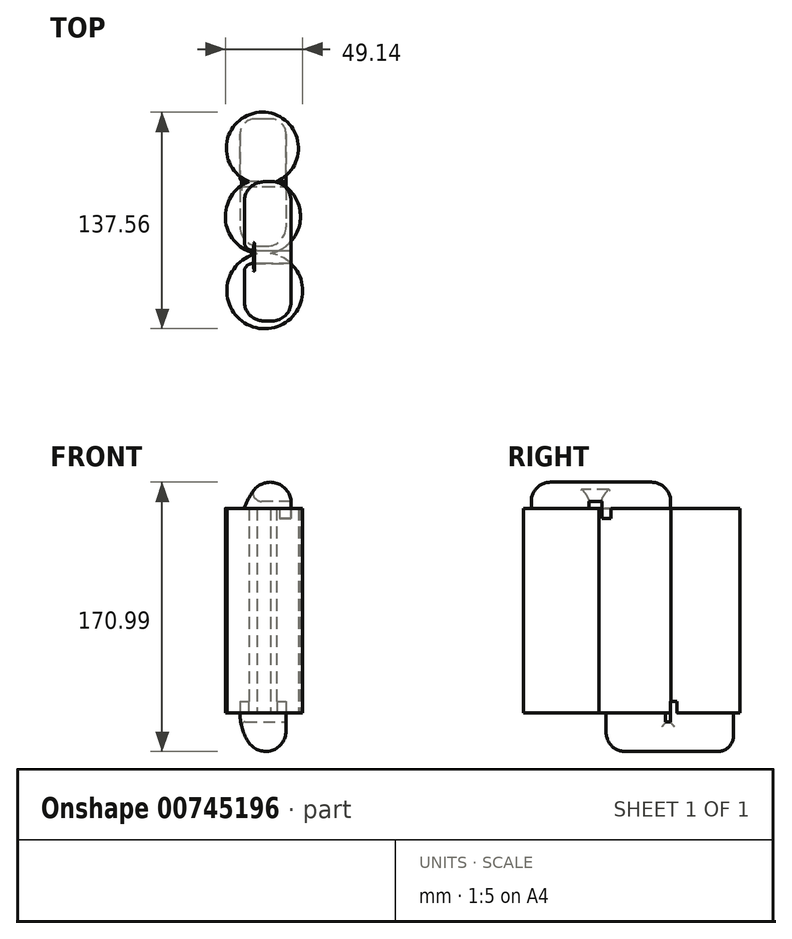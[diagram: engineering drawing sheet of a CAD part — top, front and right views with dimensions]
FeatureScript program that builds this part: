
annotation { "Feature Type Name" : "Feature", "Feature Type Description" : "" }
export const myFeature = defineFeature(function(context is Context, id is Id, definition is map)
    precondition{}
    {
        {
            var Q0;
            Q0=qCreatedBy(makeId("Top.planeOp"),FACE);
            var sketch = newSketch(context, id + "F0", { "sketchPlane" : qUnion([Q0])});
            skCircle(sketch, "E0", {"center": v(-33.88, 48.45) * mm, "radius": 22.9 * mm});
            skSolve(sketch);
        }
        {
            var Q0;
            Q0 = qSketchRegion(id + "F0", true);
            extrude(context, id + "F1", {"entities" : qUnion([Q0]), "depth" : 130 * mm, "offsetDistance" : 25 * mm});
        }
        {
            var Q0;
            Q0=qCreatedBy(makeId("Top.planeOp"),FACE);
            var sketch = newSketch(context, id + "F2", { "sketchPlane" : qUnion([Q0])});
            skCircle(sketch, "E1", {"center": v(-33.58, 5.08) * mm, "radius": 23.9 * mm});
            skSolve(sketch);
        }
        {
            var Q0;
            Q0 = qSketchRegion(id + "F2", true);
            extrude(context, id + "F3", {"entities" : qUnion([Q0]), "operationType" : NewBodyOperationType.ADD, "depth" : 105 * mm, "offsetDistance" : 25 * mm});
        }
        {
            var Q0;
            Q0=makeQuery(id+"F3.opExtrude","CAP_FACE",FACE,{"disambiguationData":[OSD([sQuery(id+"F2.wireOp",EDGE,"E1")])],"isStart":false});
            var sketch = newSketch(context, id + "F4", { "sketchPlane" : qUnion([Q0])});
            skCircle(sketch, "E2", {"center": v(-33.58, 5.08) * mm, "radius": 23.9 * mm});
            skSolve(sketch);
        }
        {
            var Q0;
            {var subQ1=makeQuery(id+"F3.boolean.opBoolean","INTERSECT",EDGE,{"derivedFrom":[makeQuery(id+"F1.opExtrude","SWEPT_FACE",FACE,{"disambiguationData":[OSD([sQuery(id+"F0.wireOp",EDGE,"E0")])]}),makeQuery(id+"F3.opExtrude","CAP_FACE",FACE,{"disambiguationData":[OSD([sQuery(id+"F2.wireOp",EDGE,"E1")])],"isStart":false})]});Q0=makeQuery(id+"F4.imprint","IMPRINT",FACE,{"disambiguationData":[TD([[makeQuery(id+"F4.imprint","IMPRINT",EDGE,{"derivedFrom":subQ1}),-1.0]])]});}
            extrude(context, id + "F5", {"entities" : qUnion([Q0]), "operationType" : NewBodyOperationType.ADD, "depth" : 25 * mm, "offsetDistance" : 25 * mm});
        }
        {
            var Q0;
            Q0=qCreatedBy(makeId("Top.planeOp"),FACE);
            var sketch = newSketch(context, id + "F6", { "sketchPlane" : qUnion([Q0])});
            skCircle(sketch, "E3", {"center": v(-32.4, -42.13) * mm, "radius": 24.08 * mm});
            skSolve(sketch);
        }
        {
            var Q0;
            Q0 = qSketchRegion(id + "F6", true);
            extrude(context, id + "F7", {"entities" : qUnion([Q0]), "operationType" : NewBodyOperationType.ADD, "depth" : 130 * mm, "offsetDistance" : 25 * mm});
        }
        {
            var Q0;
            {var subQ0=sQuery(id+"F0.wireOp",EDGE,"E0");Q0=makeQuery(id+"F7.boolean.opBoolean","MERGE",FACE,{"derivedFrom":[makeQuery(id+"F5.boolean.opBoolean","MERGE",FACE,{"derivedFrom":[makeQuery(id+"F1.opExtrude","CAP_FACE",FACE,{"disambiguationData":[OSD([subQ0])],"isStart":false}),makeQuery(id+"F5.opExtrude","CAP_FACE",FACE,{"disambiguationData":[OSD([subQ0,sQuery(id+"F2.wireOp",EDGE,"E1"),sQuery(id+"F4.wireOp",EDGE,"E2")])],"isStart":false})]}),makeQuery(id+"F7.opExtrude","CAP_FACE",FACE,{"disambiguationData":[OSD([sQuery(id+"F6.wireOp",EDGE,"E3")])],"isStart":false})]});}
            var sketch = newSketch(context, id + "F8", { "sketchPlane" : qUnion([Q0])});
            skLineSegment(sketch, "E4.bottom", {"start": v(-46.96, -61.31) * mm, "end": v(-15.68, -61.31) * mm});
            skLineSegment(sketch, "E4.top", {"start": v(-46.96, -24.82) * mm, "end": v(-15.68, -24.82) * mm});
            skLineSegment(sketch, "E4.left", {"start": v(-46.96, -61.31) * mm, "end": v(-46.96, -24.82) * mm});
            skLineSegment(sketch, "E4.right", {"start": v(-15.68, -61.31) * mm, "end": v(-15.68, -24.82) * mm});
            skSolve(sketch);
        }
        {
            var Q0;
            Q0 = qSketchRegion(id + "F8", true);
            extrude(context, id + "F9", {"entities" : qUnion([Q0]), "operationType" : NewBodyOperationType.ADD, "depth" : 28 * mm, "offsetDistance" : 25 * mm});
        }
        {
            var Q0;
            Q0=makeQuery(id+"F9.opExtrude","SWEPT_FACE",FACE,{"disambiguationData":[OSD([sQuery(id+"F8.wireOp",EDGE,"E4.top")])]});
            var sketch = newSketch(context, id + "F10", { "sketchPlane" : qUnion([Q0])});
            skLineSegment(sketch, "E5.bottom", {"start": v(15.68, 158) * mm, "end": v(46.96, 158) * mm});
            skLineSegment(sketch, "E5.top", {"start": v(15.68, 134.5) * mm, "end": v(46.96, 134.5) * mm});
            skLineSegment(sketch, "E5.left", {"start": v(15.68, 158) * mm, "end": v(15.68, 134.5) * mm});
            skLineSegment(sketch, "E5.right", {"start": v(46.96, 158) * mm, "end": v(46.96, 134.5) * mm});
            skSolve(sketch);
        }
        {
            var Q0;
            Q0 = qSketchRegion(id + "F10", true);
            extrude(context, id + "F11", {"entities" : qUnion([Q0]), "operationType" : NewBodyOperationType.ADD, "depth" : 52 * mm, "offsetDistance" : 25 * mm});
        }
        {
            var Q0;
            Q0=makeQuery(id+"F11.opExtrude","SWEPT_FACE",FACE,{"disambiguationData":[OSD([sQuery(id+"F10.wireOp",EDGE,"E5.top")])]});
            var sketch = newSketch(context, id + "F12", { "sketchPlane" : qUnion([Q0])});
            skLineSegment(sketch, "E6.bottom", {"start": v(-46.96, -27.18) * mm, "end": v(-15.68, -27.18) * mm});
            skLineSegment(sketch, "E6.top", {"start": v(-46.96, 16.43) * mm, "end": v(-15.68, 16.43) * mm});
            skLineSegment(sketch, "E6.left", {"start": v(-46.96, -27.18) * mm, "end": v(-46.96, 16.43) * mm});
            skLineSegment(sketch, "E6.right", {"start": v(-15.68, -27.18) * mm, "end": v(-15.68, 16.43) * mm});
            skSolve(sketch);
        }
        {
            var Q0;
            Q0 = qSketchRegion(id + "F12", true);
            extrude(context, id + "F13", {"entities" : qUnion([Q0]), "operationType" : NewBodyOperationType.ADD, "depth" : 11 * mm, "offsetDistance" : 25 * mm});
        }
        {
            var Q0;
            Q0=makeQuery(id+"F11.boolean.opBoolean","MERGE",EDGE,{"derivedFrom":[makeQuery(id+"F9.opExtrude","CAP_EDGE",EDGE,{"disambiguationData":[OSD([sQuery(id+"F8.wireOp",EDGE,"E4.left")])],"isStart":false}),makeQuery(id+"F11.opExtrude","SWEPT_EDGE",EDGE,{"disambiguationData":[OSD([sQuery(id+"F10.wireOp",EDGE,"E5.bottom"),sQuery(id+"F10.wireOp",EDGE,"E5.right")])]})]});
            fillet(context, id + "F14", {"entities" : qUnion([Q0]), "radius" : 41.04 * mm, "tangentPropagation" : true, "allowEdgeOverflow" : false});
        }
        {
            var Q0;
            Q0=makeQuery(id+"F7.boolean.opBoolean","MERGE",FACE,{"derivedFrom":[makeQuery(id+"F3.boolean.opBoolean","MERGE",FACE,{"derivedFrom":[makeQuery(id+"F1.opExtrude","CAP_FACE",FACE,{"disambiguationData":[OSD([sQuery(id+"F0.wireOp",EDGE,"E0")])],"isStart":true}),makeQuery(id+"F3.opExtrude","CAP_FACE",FACE,{"disambiguationData":[OSD([sQuery(id+"F2.wireOp",EDGE,"E1")])],"isStart":true})]}),makeQuery(id+"F7.opExtrude","CAP_FACE",FACE,{"disambiguationData":[OSD([sQuery(id+"F6.wireOp",EDGE,"E3")])],"isStart":true})]});
            var sketch = newSketch(context, id + "F15", { "sketchPlane" : qUnion([Q0])});
            skLineSegment(sketch, "E7.bottom", {"start": v(-48.12, -24.03) * mm, "end": v(-18.9, -24.03) * mm});
            skLineSegment(sketch, "E7.top", {"start": v(-48.12, 13.78) * mm, "end": v(-18.9, 13.78) * mm});
            skLineSegment(sketch, "E7.left", {"start": v(-48.12, -24.03) * mm, "end": v(-48.12, 13.78) * mm});
            skLineSegment(sketch, "E7.right", {"start": v(-18.9, -24.03) * mm, "end": v(-18.9, 13.78) * mm});
            skSolve(sketch);
        }
        {
            var Q0;
            Q0 = qSketchRegion(id + "F15", true);
            extrude(context, id + "F16", {"entities" : qUnion([Q0]), "operationType" : NewBodyOperationType.ADD, "depth" : 32 * mm, "offsetDistance" : 25 * mm});
        }
        {
            var Q0;
            Q0=makeQuery(id+"F16.opExtrude","SWEPT_FACE",FACE,{"disambiguationData":[OSD([sQuery(id+"F15.wireOp",EDGE,"E7.bottom")])]});
            var sketch = newSketch(context, id + "F17", { "sketchPlane" : qUnion([Q0])});
            skLineSegment(sketch, "E8.bottom", {"start": v(48.12, -32) * mm, "end": v(18.9, -32) * mm});
            skLineSegment(sketch, "E8.top", {"start": v(48.12, -5.6) * mm, "end": v(18.9, -5.6) * mm});
            skLineSegment(sketch, "E8.left", {"start": v(48.12, -32) * mm, "end": v(48.12, -5.6) * mm});
            skLineSegment(sketch, "E8.right", {"start": v(18.9, -32) * mm, "end": v(18.9, -5.6) * mm});
            skSolve(sketch);
        }
        {
            var Q0;
            Q0 = qSketchRegion(id + "F17", true);
            extrude(context, id + "F18", {"entities" : qUnion([Q0]), "operationType" : NewBodyOperationType.ADD, "depth" : 43 * mm, "offsetDistance" : 25 * mm});
        }
        {
            var Q0;
            Q0=makeQuery(id+"F18.opExtrude","SWEPT_FACE",FACE,{"disambiguationData":[OSD([sQuery(id+"F17.wireOp",EDGE,"E8.top")])]});
            var sketch = newSketch(context, id + "F19", { "sketchPlane" : qUnion([Q0])});
            skLineSegment(sketch, "E9.bottom", {"start": v(-48.12, 67.03) * mm, "end": v(-18.9, 67.03) * mm});
            skLineSegment(sketch, "E9.top", {"start": v(-48.12, 27.18) * mm, "end": v(-18.9, 27.18) * mm});
            skLineSegment(sketch, "E9.left", {"start": v(-48.12, 67.03) * mm, "end": v(-48.12, 27.18) * mm});
            skLineSegment(sketch, "E9.right", {"start": v(-18.9, 67.03) * mm, "end": v(-18.9, 27.18) * mm});
            skSolve(sketch);
        }
        {
            var Q0;
            Q0 = qSketchRegion(id + "F19", true);
            extrude(context, id + "F20", {"entities" : qUnion([Q0]), "operationType" : NewBodyOperationType.ADD, "depth" : 13 * mm, "offsetDistance" : 25 * mm});
        }
        {
            var Q0;
            Q0=makeQuery(id+"F18.boolean.opBoolean","MERGE",EDGE,{"derivedFrom":[makeQuery(id+"F16.opExtrude","CAP_EDGE",EDGE,{"disambiguationData":[OSD([sQuery(id+"F15.wireOp",EDGE,"E7.left")])],"isStart":false}),makeQuery(id+"F18.opExtrude","SWEPT_EDGE",EDGE,{"disambiguationData":[OSD([sQuery(id+"F17.wireOp",EDGE,"E8.bottom"),sQuery(id+"F17.wireOp",EDGE,"E8.left")])]})]});
            fillet(context, id + "F21", {"entities" : qUnion([Q0]), "radius" : 31.38 * mm, "tangentPropagation" : true, "allowEdgeOverflow" : false});
        }
        {
            var Q0;
            Q0=makeQuery(id+"F21.opFillet","BLEND_EDGE",EDGE,{"blendedFrom":[makeQuery(id+"F18.boolean.opBoolean","MERGE",EDGE,{"derivedFrom":[makeQuery(id+"F16.opExtrude","CAP_EDGE",EDGE,{"disambiguationData":[OSD([sQuery(id+"F15.wireOp",EDGE,"E7.left")])],"isStart":false}),makeQuery(id+"F18.opExtrude","SWEPT_EDGE",EDGE,{"disambiguationData":[OSD([sQuery(id+"F17.wireOp",EDGE,"E8.bottom"),sQuery(id+"F17.wireOp",EDGE,"E8.left")])]})]}),makeQuery(id+"F20.boolean.opBoolean","MERGE",FACE,{"derivedFrom":[makeQuery(id+"F18.boolean.opBoolean","MERGE",FACE,{"derivedFrom":[makeQuery(id+"F16.opExtrude","SWEPT_FACE",FACE,{"disambiguationData":[OSD([sQuery(id+"F15.wireOp",EDGE,"E7.right")])]}),makeQuery(id+"F18.opExtrude","SWEPT_FACE",FACE,{"disambiguationData":[OSD([sQuery(id+"F17.wireOp",EDGE,"E8.right")])]})]}),makeQuery(id+"F20.opExtrude","SWEPT_FACE",FACE,{"disambiguationData":[OSD([sQuery(id+"F19.wireOp",EDGE,"E9.right")])]})]})],"blendedInto":[makeQuery(id+"F20.boolean.opBoolean","MERGE",FACE,{"derivedFrom":[makeQuery(id+"F18.boolean.opBoolean","MERGE",FACE,{"derivedFrom":[makeQuery(id+"F16.opExtrude","SWEPT_FACE",FACE,{"disambiguationData":[OSD([sQuery(id+"F15.wireOp",EDGE,"E7.right")])]}),makeQuery(id+"F18.opExtrude","SWEPT_FACE",FACE,{"disambiguationData":[OSD([sQuery(id+"F17.wireOp",EDGE,"E8.right")])]})]}),makeQuery(id+"F20.opExtrude","SWEPT_FACE",FACE,{"disambiguationData":[OSD([sQuery(id+"F19.wireOp",EDGE,"E9.right")])]})]})]});
            fillet(context, id + "F22", {"entities" : qUnion([Q0]), "radius" : 12.9 * mm, "tangentPropagation" : true, "allowEdgeOverflow" : false});
        }
        {
            var Q0;
            {var subQ0=sQuery(id+"F17.wireOp",EDGE,"E8.right");var subQ1=sQuery(id+"F17.wireOp",EDGE,"E8.left");var subQ2=sQuery(id+"F17.wireOp",EDGE,"E8.bottom");Q0=makeQuery(id+"F22.opFillet","BLEND_EDGE",EDGE,{"blendedFrom":[makeQuery(id+"F21.opFillet","BLEND_EDGE",EDGE,{"blendedFrom":[makeQuery(id+"F18.boolean.opBoolean","MERGE",EDGE,{"derivedFrom":[makeQuery(id+"F16.opExtrude","CAP_EDGE",EDGE,{"disambiguationData":[OSD([sQuery(id+"F15.wireOp",EDGE,"E7.left")])],"isStart":false}),makeQuery(id+"F18.opExtrude","SWEPT_EDGE",EDGE,{"disambiguationData":[OSD([subQ2,subQ1])]})]}),makeQuery(id+"F20.boolean.opBoolean","MERGE",FACE,{"derivedFrom":[makeQuery(id+"F18.boolean.opBoolean","MERGE",FACE,{"derivedFrom":[makeQuery(id+"F16.opExtrude","SWEPT_FACE",FACE,{"disambiguationData":[OSD([sQuery(id+"F15.wireOp",EDGE,"E7.right")])]}),makeQuery(id+"F18.opExtrude","SWEPT_FACE",FACE,{"disambiguationData":[OSD([subQ0])]})]}),makeQuery(id+"F20.opExtrude","SWEPT_FACE",FACE,{"disambiguationData":[OSD([sQuery(id+"F19.wireOp",EDGE,"E9.right")])]})]})],"blendedInto":[makeQuery(id+"F20.boolean.opBoolean","MERGE",FACE,{"derivedFrom":[makeQuery(id+"F18.boolean.opBoolean","MERGE",FACE,{"derivedFrom":[makeQuery(id+"F16.opExtrude","SWEPT_FACE",FACE,{"disambiguationData":[OSD([sQuery(id+"F15.wireOp",EDGE,"E7.right")])]}),makeQuery(id+"F18.opExtrude","SWEPT_FACE",FACE,{"disambiguationData":[OSD([subQ0])]})]}),makeQuery(id+"F20.opExtrude","SWEPT_FACE",FACE,{"disambiguationData":[OSD([sQuery(id+"F19.wireOp",EDGE,"E9.right")])]})]})]}),makeQuery(id+"F20.boolean.opBoolean","MERGE",FACE,{"derivedFrom":[makeQuery(id+"F18.opExtrude","CAP_FACE",FACE,{"disambiguationData":[OSD([subQ2,sQuery(id+"F17.wireOp",EDGE,"E8.top"),subQ1,subQ0])],"isStart":false}),makeQuery(id+"F20.opExtrude","SWEPT_FACE",FACE,{"disambiguationData":[OSD([sQuery(id+"F19.wireOp",EDGE,"E9.bottom")])]})]})],"blendedInto":[makeQuery(id+"F20.boolean.opBoolean","MERGE",FACE,{"derivedFrom":[makeQuery(id+"F18.opExtrude","CAP_FACE",FACE,{"disambiguationData":[OSD([subQ2,sQuery(id+"F17.wireOp",EDGE,"E8.top"),subQ1,subQ0])],"isStart":false}),makeQuery(id+"F20.opExtrude","SWEPT_FACE",FACE,{"disambiguationData":[OSD([sQuery(id+"F19.wireOp",EDGE,"E9.bottom")])]})]})]});}
            fillet(context, id + "F23", {"entities" : qUnion([Q0]), "radius" : 9.66 * mm, "tangentPropagation" : true, "allowEdgeOverflow" : false});
        }
        {
            var Q0;
            Q0=makeQuery(id+"F22.opFillet","BLEND_EDGE",EDGE,{"blendedFrom":[makeQuery(id+"F21.opFillet","BLEND_EDGE",EDGE,{"blendedFrom":[makeQuery(id+"F18.boolean.opBoolean","MERGE",EDGE,{"derivedFrom":[makeQuery(id+"F16.opExtrude","CAP_EDGE",EDGE,{"disambiguationData":[OSD([sQuery(id+"F15.wireOp",EDGE,"E7.left")])],"isStart":false}),makeQuery(id+"F18.opExtrude","SWEPT_EDGE",EDGE,{"disambiguationData":[OSD([sQuery(id+"F17.wireOp",EDGE,"E8.bottom"),sQuery(id+"F17.wireOp",EDGE,"E8.left")])]})]}),makeQuery(id+"F20.boolean.opBoolean","MERGE",FACE,{"derivedFrom":[makeQuery(id+"F18.boolean.opBoolean","MERGE",FACE,{"derivedFrom":[makeQuery(id+"F16.opExtrude","SWEPT_FACE",FACE,{"disambiguationData":[OSD([sQuery(id+"F15.wireOp",EDGE,"E7.right")])]}),makeQuery(id+"F18.opExtrude","SWEPT_FACE",FACE,{"disambiguationData":[OSD([sQuery(id+"F17.wireOp",EDGE,"E8.right")])]})]}),makeQuery(id+"F20.opExtrude","SWEPT_FACE",FACE,{"disambiguationData":[OSD([sQuery(id+"F19.wireOp",EDGE,"E9.right")])]})]})],"blendedInto":[makeQuery(id+"F20.boolean.opBoolean","MERGE",FACE,{"derivedFrom":[makeQuery(id+"F18.boolean.opBoolean","MERGE",FACE,{"derivedFrom":[makeQuery(id+"F16.opExtrude","SWEPT_FACE",FACE,{"disambiguationData":[OSD([sQuery(id+"F15.wireOp",EDGE,"E7.right")])]}),makeQuery(id+"F18.opExtrude","SWEPT_FACE",FACE,{"disambiguationData":[OSD([sQuery(id+"F17.wireOp",EDGE,"E8.right")])]})]}),makeQuery(id+"F20.opExtrude","SWEPT_FACE",FACE,{"disambiguationData":[OSD([sQuery(id+"F19.wireOp",EDGE,"E9.right")])]})]})]}),makeQuery(id+"F16.opExtrude","SWEPT_FACE",FACE,{"disambiguationData":[OSD([sQuery(id+"F15.wireOp",EDGE,"E7.top")])]})],"blendedInto":[makeQuery(id+"F16.opExtrude","SWEPT_FACE",FACE,{"disambiguationData":[OSD([sQuery(id+"F15.wireOp",EDGE,"E7.top")])]})]});
            fillet(context, id + "F24", {"entities" : qUnion([Q0]), "radius" : 12.07 * mm, "tangentPropagation" : true, "allowEdgeOverflow" : false});
        }
        {
            var Q0;
            Q0=makeQuery(id+"F14.opFillet","BLEND_EDGE",EDGE,{"blendedFrom":[makeQuery(id+"F11.boolean.opBoolean","MERGE",EDGE,{"derivedFrom":[makeQuery(id+"F9.opExtrude","CAP_EDGE",EDGE,{"disambiguationData":[OSD([sQuery(id+"F8.wireOp",EDGE,"E4.left")])],"isStart":false}),makeQuery(id+"F11.opExtrude","SWEPT_EDGE",EDGE,{"disambiguationData":[OSD([sQuery(id+"F10.wireOp",EDGE,"E5.bottom"),sQuery(id+"F10.wireOp",EDGE,"E5.right")])]})]}),makeQuery(id+"F13.boolean.opBoolean","MERGE",FACE,{"derivedFrom":[makeQuery(id+"F11.boolean.opBoolean","MERGE",FACE,{"derivedFrom":[makeQuery(id+"F9.opExtrude","SWEPT_FACE",FACE,{"disambiguationData":[OSD([sQuery(id+"F8.wireOp",EDGE,"E4.right")])]}),makeQuery(id+"F11.opExtrude","SWEPT_FACE",FACE,{"disambiguationData":[OSD([sQuery(id+"F10.wireOp",EDGE,"E5.left")])]})]}),makeQuery(id+"F13.opExtrude","SWEPT_FACE",FACE,{"disambiguationData":[OSD([sQuery(id+"F12.wireOp",EDGE,"E6.right")])]})]})],"blendedInto":[makeQuery(id+"F13.boolean.opBoolean","MERGE",FACE,{"derivedFrom":[makeQuery(id+"F11.boolean.opBoolean","MERGE",FACE,{"derivedFrom":[makeQuery(id+"F9.opExtrude","SWEPT_FACE",FACE,{"disambiguationData":[OSD([sQuery(id+"F8.wireOp",EDGE,"E4.right")])]}),makeQuery(id+"F11.opExtrude","SWEPT_FACE",FACE,{"disambiguationData":[OSD([sQuery(id+"F10.wireOp",EDGE,"E5.left")])]})]}),makeQuery(id+"F13.opExtrude","SWEPT_FACE",FACE,{"disambiguationData":[OSD([sQuery(id+"F12.wireOp",EDGE,"E6.right")])]})]})]});
            fillet(context, id + "F25", {"entities" : qUnion([Q0]), "radius" : 13.2 * mm, "tangentPropagation" : true, "allowEdgeOverflow" : false});
        }
        {
            var Q0;
            {var subQ0=sQuery(id+"F10.wireOp",EDGE,"E5.right");var subQ1=sQuery(id+"F10.wireOp",EDGE,"E5.left");var subQ2=sQuery(id+"F10.wireOp",EDGE,"E5.bottom");Q0=makeQuery(id+"F25.opFillet","BLEND_EDGE",EDGE,{"blendedFrom":[makeQuery(id+"F14.opFillet","BLEND_EDGE",EDGE,{"blendedFrom":[makeQuery(id+"F11.boolean.opBoolean","MERGE",EDGE,{"derivedFrom":[makeQuery(id+"F9.opExtrude","CAP_EDGE",EDGE,{"disambiguationData":[OSD([sQuery(id+"F8.wireOp",EDGE,"E4.left")])],"isStart":false}),makeQuery(id+"F11.opExtrude","SWEPT_EDGE",EDGE,{"disambiguationData":[OSD([subQ2,subQ0])]})]}),makeQuery(id+"F13.boolean.opBoolean","MERGE",FACE,{"derivedFrom":[makeQuery(id+"F11.boolean.opBoolean","MERGE",FACE,{"derivedFrom":[makeQuery(id+"F9.opExtrude","SWEPT_FACE",FACE,{"disambiguationData":[OSD([sQuery(id+"F8.wireOp",EDGE,"E4.right")])]}),makeQuery(id+"F11.opExtrude","SWEPT_FACE",FACE,{"disambiguationData":[OSD([subQ1])]})]}),makeQuery(id+"F13.opExtrude","SWEPT_FACE",FACE,{"disambiguationData":[OSD([sQuery(id+"F12.wireOp",EDGE,"E6.right")])]})]})],"blendedInto":[makeQuery(id+"F13.boolean.opBoolean","MERGE",FACE,{"derivedFrom":[makeQuery(id+"F11.boolean.opBoolean","MERGE",FACE,{"derivedFrom":[makeQuery(id+"F9.opExtrude","SWEPT_FACE",FACE,{"disambiguationData":[OSD([sQuery(id+"F8.wireOp",EDGE,"E4.right")])]}),makeQuery(id+"F11.opExtrude","SWEPT_FACE",FACE,{"disambiguationData":[OSD([subQ1])]})]}),makeQuery(id+"F13.opExtrude","SWEPT_FACE",FACE,{"disambiguationData":[OSD([sQuery(id+"F12.wireOp",EDGE,"E6.right")])]})]})]}),makeQuery(id+"F13.boolean.opBoolean","MERGE",FACE,{"derivedFrom":[makeQuery(id+"F11.opExtrude","CAP_FACE",FACE,{"disambiguationData":[OSD([subQ2,sQuery(id+"F10.wireOp",EDGE,"E5.top"),subQ1,subQ0])],"isStart":false}),makeQuery(id+"F13.opExtrude","SWEPT_FACE",FACE,{"disambiguationData":[OSD([sQuery(id+"F12.wireOp",EDGE,"E6.bottom")])]})]})],"blendedInto":[makeQuery(id+"F13.boolean.opBoolean","MERGE",FACE,{"derivedFrom":[makeQuery(id+"F11.opExtrude","CAP_FACE",FACE,{"disambiguationData":[OSD([subQ2,sQuery(id+"F10.wireOp",EDGE,"E5.top"),subQ1,subQ0])],"isStart":false}),makeQuery(id+"F13.opExtrude","SWEPT_FACE",FACE,{"disambiguationData":[OSD([sQuery(id+"F12.wireOp",EDGE,"E6.bottom")])]})]})]});}
            fillet(context, id + "F26", {"entities" : qUnion([Q0]), "radius" : 12.07 * mm, "tangentPropagation" : true, "allowEdgeOverflow" : false});
        }
        {
            var Q0;
            Q0=makeQuery(id+"F25.opFillet","BLEND_EDGE",EDGE,{"blendedFrom":[makeQuery(id+"F14.opFillet","BLEND_EDGE",EDGE,{"blendedFrom":[makeQuery(id+"F11.boolean.opBoolean","MERGE",EDGE,{"derivedFrom":[makeQuery(id+"F9.opExtrude","CAP_EDGE",EDGE,{"disambiguationData":[OSD([sQuery(id+"F8.wireOp",EDGE,"E4.left")])],"isStart":false}),makeQuery(id+"F11.opExtrude","SWEPT_EDGE",EDGE,{"disambiguationData":[OSD([sQuery(id+"F10.wireOp",EDGE,"E5.bottom"),sQuery(id+"F10.wireOp",EDGE,"E5.right")])]})]}),makeQuery(id+"F13.boolean.opBoolean","MERGE",FACE,{"derivedFrom":[makeQuery(id+"F11.boolean.opBoolean","MERGE",FACE,{"derivedFrom":[makeQuery(id+"F9.opExtrude","SWEPT_FACE",FACE,{"disambiguationData":[OSD([sQuery(id+"F8.wireOp",EDGE,"E4.right")])]}),makeQuery(id+"F11.opExtrude","SWEPT_FACE",FACE,{"disambiguationData":[OSD([sQuery(id+"F10.wireOp",EDGE,"E5.left")])]})]}),makeQuery(id+"F13.opExtrude","SWEPT_FACE",FACE,{"disambiguationData":[OSD([sQuery(id+"F12.wireOp",EDGE,"E6.right")])]})]})],"blendedInto":[makeQuery(id+"F13.boolean.opBoolean","MERGE",FACE,{"derivedFrom":[makeQuery(id+"F11.boolean.opBoolean","MERGE",FACE,{"derivedFrom":[makeQuery(id+"F9.opExtrude","SWEPT_FACE",FACE,{"disambiguationData":[OSD([sQuery(id+"F8.wireOp",EDGE,"E4.right")])]}),makeQuery(id+"F11.opExtrude","SWEPT_FACE",FACE,{"disambiguationData":[OSD([sQuery(id+"F10.wireOp",EDGE,"E5.left")])]})]}),makeQuery(id+"F13.opExtrude","SWEPT_FACE",FACE,{"disambiguationData":[OSD([sQuery(id+"F12.wireOp",EDGE,"E6.right")])]})]})]}),makeQuery(id+"F9.opExtrude","SWEPT_FACE",FACE,{"disambiguationData":[OSD([sQuery(id+"F8.wireOp",EDGE,"E4.bottom")])]})],"blendedInto":[makeQuery(id+"F9.opExtrude","SWEPT_FACE",FACE,{"disambiguationData":[OSD([sQuery(id+"F8.wireOp",EDGE,"E4.bottom")])]})]});
            fillet(context, id + "F27", {"entities" : qUnion([Q0]), "radius" : 12.07 * mm, "tangentPropagation" : true, "allowEdgeOverflow" : false});
        }
        {
            var Q0;
            Q0=makeQuery(id+"F21.opFillet","BLEND_EDGE",EDGE,{"blendedFrom":[makeQuery(id+"F18.boolean.opBoolean","MERGE",EDGE,{"derivedFrom":[makeQuery(id+"F16.opExtrude","CAP_EDGE",EDGE,{"disambiguationData":[OSD([sQuery(id+"F15.wireOp",EDGE,"E7.left")])],"isStart":false}),makeQuery(id+"F18.opExtrude","SWEPT_EDGE",EDGE,{"disambiguationData":[OSD([sQuery(id+"F17.wireOp",EDGE,"E8.bottom"),sQuery(id+"F17.wireOp",EDGE,"E8.left")])]})]}),makeQuery(id+"F16.opExtrude","SWEPT_FACE",FACE,{"disambiguationData":[OSD([sQuery(id+"F15.wireOp",EDGE,"E7.bottom")])]})],"blendedInto":[makeQuery(id+"F16.opExtrude","SWEPT_FACE",FACE,{"disambiguationData":[OSD([sQuery(id+"F15.wireOp",EDGE,"E7.bottom")])]})]});
            var Q1;
            Q1=makeQuery(id+"F21.opFillet","BLEND_EDGE",EDGE,{"blendedFrom":[makeQuery(id+"F18.boolean.opBoolean","MERGE",EDGE,{"derivedFrom":[makeQuery(id+"F16.opExtrude","CAP_EDGE",EDGE,{"disambiguationData":[OSD([sQuery(id+"F15.wireOp",EDGE,"E7.left")])],"isStart":false}),makeQuery(id+"F18.opExtrude","SWEPT_EDGE",EDGE,{"disambiguationData":[OSD([sQuery(id+"F17.wireOp",EDGE,"E8.bottom"),sQuery(id+"F17.wireOp",EDGE,"E8.left")])]})]}),makeQuery(id+"F18.opExtrude","SWEPT_FACE",FACE,{"disambiguationData":[OSD([sQuery(id+"F17.wireOp",EDGE,"E8.top")])]})],"blendedInto":[makeQuery(id+"F18.opExtrude","SWEPT_FACE",FACE,{"disambiguationData":[OSD([sQuery(id+"F17.wireOp",EDGE,"E8.top")])]})]});
            var Q2;
            Q2=makeQuery(id+"F21.opFillet","BLEND_EDGE",EDGE,{"blendedFrom":[makeQuery(id+"F18.boolean.opBoolean","MERGE",EDGE,{"derivedFrom":[makeQuery(id+"F16.opExtrude","CAP_EDGE",EDGE,{"disambiguationData":[OSD([sQuery(id+"F15.wireOp",EDGE,"E7.left")])],"isStart":false}),makeQuery(id+"F18.opExtrude","SWEPT_EDGE",EDGE,{"disambiguationData":[OSD([sQuery(id+"F17.wireOp",EDGE,"E8.bottom"),sQuery(id+"F17.wireOp",EDGE,"E8.left")])]})]}),makeQuery(id+"F20.opExtrude","SWEPT_FACE",FACE,{"disambiguationData":[OSD([sQuery(id+"F19.wireOp",EDGE,"E9.top")])]})],"blendedInto":[makeQuery(id+"F20.opExtrude","SWEPT_FACE",FACE,{"disambiguationData":[OSD([sQuery(id+"F19.wireOp",EDGE,"E9.top")])]})]});
            fillet(context, id + "F28", {"entities" : qUnion([Q0, Q1, Q2]), "radius" : 2.41 * mm, "tangentPropagation" : true, "allowEdgeOverflow" : false});
        }
        {
            var Q0;
            Q0=makeQuery(id+"F14.opFillet","BLEND_EDGE",EDGE,{"blendedFrom":[makeQuery(id+"F11.boolean.opBoolean","MERGE",EDGE,{"derivedFrom":[makeQuery(id+"F9.opExtrude","CAP_EDGE",EDGE,{"disambiguationData":[OSD([sQuery(id+"F8.wireOp",EDGE,"E4.left")])],"isStart":false}),makeQuery(id+"F11.opExtrude","SWEPT_EDGE",EDGE,{"disambiguationData":[OSD([sQuery(id+"F10.wireOp",EDGE,"E5.bottom"),sQuery(id+"F10.wireOp",EDGE,"E5.right")])]})]}),makeQuery(id+"F13.opExtrude","SWEPT_FACE",FACE,{"disambiguationData":[OSD([sQuery(id+"F12.wireOp",EDGE,"E6.top")])]})],"blendedInto":[makeQuery(id+"F13.opExtrude","SWEPT_FACE",FACE,{"disambiguationData":[OSD([sQuery(id+"F12.wireOp",EDGE,"E6.top")])]})]});
            var Q1;
            Q1=makeQuery(id+"F14.opFillet","BLEND_EDGE",EDGE,{"blendedFrom":[makeQuery(id+"F11.boolean.opBoolean","MERGE",EDGE,{"derivedFrom":[makeQuery(id+"F9.opExtrude","CAP_EDGE",EDGE,{"disambiguationData":[OSD([sQuery(id+"F8.wireOp",EDGE,"E4.left")])],"isStart":false}),makeQuery(id+"F11.opExtrude","SWEPT_EDGE",EDGE,{"disambiguationData":[OSD([sQuery(id+"F10.wireOp",EDGE,"E5.bottom"),sQuery(id+"F10.wireOp",EDGE,"E5.right")])]})]}),makeQuery(id+"F11.opExtrude","SWEPT_FACE",FACE,{"disambiguationData":[OSD([sQuery(id+"F10.wireOp",EDGE,"E5.top")])]})],"blendedInto":[makeQuery(id+"F11.opExtrude","SWEPT_FACE",FACE,{"disambiguationData":[OSD([sQuery(id+"F10.wireOp",EDGE,"E5.top")])]})]});
            var Q2;
            Q2=makeQuery(id+"F14.opFillet","BLEND_EDGE",EDGE,{"blendedFrom":[makeQuery(id+"F11.boolean.opBoolean","MERGE",EDGE,{"derivedFrom":[makeQuery(id+"F9.opExtrude","CAP_EDGE",EDGE,{"disambiguationData":[OSD([sQuery(id+"F8.wireOp",EDGE,"E4.left")])],"isStart":false}),makeQuery(id+"F11.opExtrude","SWEPT_EDGE",EDGE,{"disambiguationData":[OSD([sQuery(id+"F10.wireOp",EDGE,"E5.bottom"),sQuery(id+"F10.wireOp",EDGE,"E5.right")])]})]}),makeQuery(id+"F9.opExtrude","SWEPT_FACE",FACE,{"disambiguationData":[OSD([sQuery(id+"F8.wireOp",EDGE,"E4.top")])]})],"blendedInto":[makeQuery(id+"F9.opExtrude","SWEPT_FACE",FACE,{"disambiguationData":[OSD([sQuery(id+"F8.wireOp",EDGE,"E4.top")])]})]});
            fillet(context, id + "F29", {"entities" : qUnion([Q0, Q1, Q2]), "radius" : 5 * mm, "tangentPropagation" : true, "allowEdgeOverflow" : false});
        }
    });
